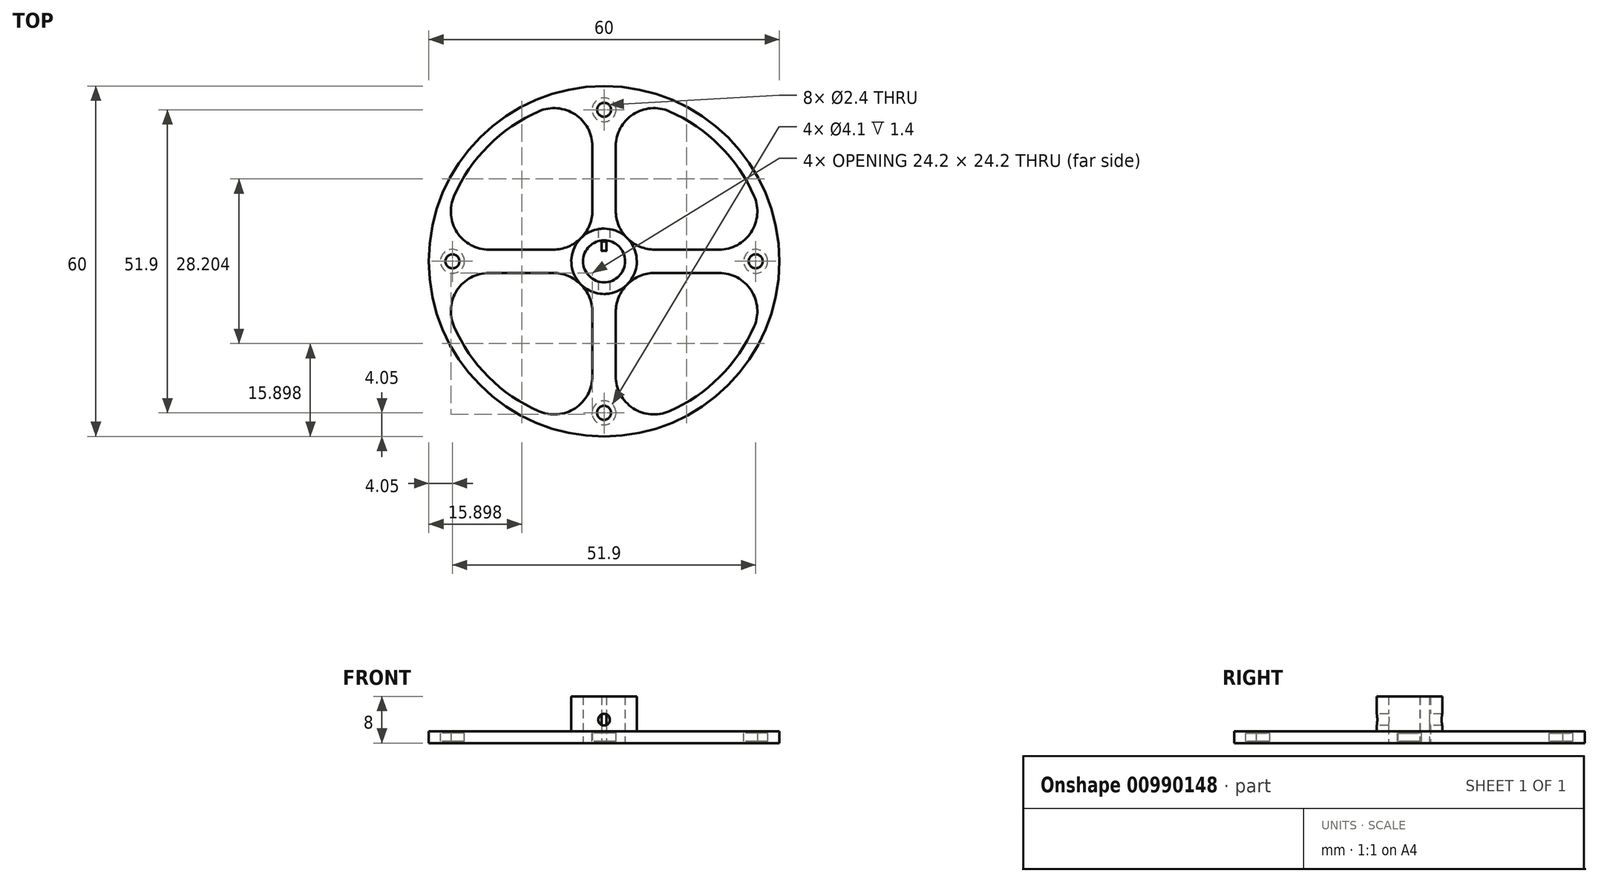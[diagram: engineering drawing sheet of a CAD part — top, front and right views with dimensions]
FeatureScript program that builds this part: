
annotation { "Feature Type Name" : "Feature", "Feature Type Description" : "" }
export const myFeature = defineFeature(function(context is Context, id is Id, definition is map)
    precondition{}
    {
        {
            assignVariable(context, id + "F0", {"name" : "Diameter", "anyValue" : 60 * mm});
        }
        {
            assignVariable(context, id + "F1", {"name" : "Buffer", "anyValue" : 2 * mm});
        }
        {
            assignVariable(context, id + "F2", {"name" : "BushingThickness", "anyValue" : 1.4 * mm});
        }
        {
            var Q0;
            Q0=qCreatedBy(makeId("Top.planeOp"),FACE);
            var sketch = newSketch(context, id + "F3", { "sketchPlane" : qUnion([Q0])});
            skCircle(sketch, "E0", {"center": v(0, 0) * mm, "radius": 30 * mm});
            skCircle(sketch, "E1", {"center": v(0, 0) * mm, "radius": 1.6 * mm});
            skCircle(sketch, "E2", {"center": v(0, 0) * mm, "radius": 3.6 * mm});
            skCircle(sketch, "E3", {"center": v(0, 0) * mm, "radius": 5.6 * mm});
            skCircle(sketch, "E4", {"center": v(-25.95, 0) * mm, "radius": 2.05 * mm});
            skCircle(sketch, "E5", {"center": v(-25.95, 0) * mm, "radius": 4.05 * mm});
            skLineSegment(sketch, "E6", {"start": v(-22.43, 2) * mm, "end": v(-5.23, 2) * mm});
            skLineSegment(sketch, "E7", {"start": v(-22.43, -2) * mm, "end": v(-5.23, -2) * mm});
            skCircle(sketch, "E8", {"center": v(0, 0) * mm, "radius": 28 * mm});
            skCircle(sketch, "E9", {"center": v(-19.69, 8.54) * mm, "radius": 6.54 * mm});
            skCircle(sketch, "E10", {"center": v(-8.7, 8.7) * mm, "radius": 6.7 * mm});
            skCircle(sketch, "E11", {"center": v(-19.69, -8.54) * mm, "radius": 6.54 * mm});
            skLineSegment(sketch, "E12", {"start": v(0, 0) * mm, "end": v(-21.21, 21.21) * mm});
            skCircle(sketch, "E13.1.0", {"center": v(-8.7, -8.7) * mm, "radius": 6.7 * mm});
            skCircle(sketch, "E13.1.1", {"center": v(-8.54, -19.69) * mm, "radius": 6.54 * mm});
            skLineSegment(sketch, "E13.1.2", {"start": v(0, 0) * mm, "end": v(-21.21, -21.21) * mm});
            skCircle(sketch, "E13.1.3", {"center": v(0, -25.95) * mm, "radius": 4.05 * mm});
            skCircle(sketch, "E13.1.4", {"center": v(0, -25.95) * mm, "radius": 2.05 * mm});
            skCircle(sketch, "E13.1.5", {"center": v(8.54, -19.69) * mm, "radius": 6.54 * mm});
            skLineSegment(sketch, "E13.1.6", {"start": v(2, -22.43) * mm, "end": v(2, -5.23) * mm});
            skLineSegment(sketch, "E13.1.7", {"start": v(-2, -22.43) * mm, "end": v(-2, -5.23) * mm});
            skCircle(sketch, "E13.2.0", {"center": v(8.7, -8.7) * mm, "radius": 6.7 * mm});
            skCircle(sketch, "E13.2.1", {"center": v(19.69, -8.54) * mm, "radius": 6.54 * mm});
            skLineSegment(sketch, "E13.2.2", {"start": v(0, 0) * mm, "end": v(21.21, -21.21) * mm});
            skCircle(sketch, "E13.2.3", {"center": v(25.95, 0) * mm, "radius": 4.05 * mm});
            skCircle(sketch, "E13.2.4", {"center": v(25.95, 0) * mm, "radius": 2.05 * mm});
            skCircle(sketch, "E13.2.5", {"center": v(19.69, 8.54) * mm, "radius": 6.54 * mm});
            skLineSegment(sketch, "E13.2.6", {"start": v(22.43, 2) * mm, "end": v(5.23, 2) * mm});
            skLineSegment(sketch, "E13.2.7", {"start": v(22.43, -2) * mm, "end": v(5.23, -2) * mm});
            skCircle(sketch, "E13.3.0", {"center": v(8.7, 8.7) * mm, "radius": 6.7 * mm});
            skCircle(sketch, "E13.3.1", {"center": v(8.54, 19.69) * mm, "radius": 6.54 * mm});
            skLineSegment(sketch, "E13.3.2", {"start": v(0, 0) * mm, "end": v(21.21, 21.21) * mm});
            skCircle(sketch, "E13.3.3", {"center": v(0, 25.95) * mm, "radius": 4.05 * mm});
            skCircle(sketch, "E13.3.4", {"center": v(0, 25.95) * mm, "radius": 2.05 * mm});
            skCircle(sketch, "E13.3.5", {"center": v(-8.54, 19.69) * mm, "radius": 6.54 * mm});
            skLineSegment(sketch, "E13.3.6", {"start": v(-2, 22.43) * mm, "end": v(-2, 5.23) * mm});
            skLineSegment(sketch, "E13.3.7", {"start": v(2, 22.43) * mm, "end": v(2, 5.23) * mm});
            skCircle(sketch, "E14", {"center": v(-25.95, 0) * mm, "radius": 1.2 * mm});
            skCircle(sketch, "E15.1.0", {"center": v(0, -25.95) * mm, "radius": 1.2 * mm});
            skCircle(sketch, "E15.2.0", {"center": v(25.95, 0) * mm, "radius": 1.2 * mm});
            skCircle(sketch, "E15.3.0", {"center": v(0, 25.95) * mm, "radius": 1.2 * mm});
            skSolve(sketch);
        }
        {
            var Q0;
            {var subQ4=sQuery(id+"F3.wireOp",EDGE,"E12");var subQ6=sQuery(id+"F3.wireOp",EDGE,"E0");var subQ8=makeQuery(id+"F3.imprint","INTERSECT",VERTEX,{"derivedFrom":[subQ6,subQ4]});Q0=makeQuery(id+"F3.imprint","IMPRINT",FACE,{"disambiguationData":[TD([[makeQuery(id+"F3.imprint","IMPRINT",EDGE,{"disambiguationData":[TD([[subQ8,-1.0]])],"derivedFrom":subQ6}),1.0]])]});}
            var Q1;
            {var subQ2=sQuery(id+"F3.wireOp",EDGE,"E13.1.2");var subQ6=sQuery(id+"F3.wireOp",EDGE,"E0");var subQ8=makeQuery(id+"F3.imprint","INTERSECT",VERTEX,{"derivedFrom":[subQ6,subQ2]});Q1=makeQuery(id+"F3.imprint","IMPRINT",FACE,{"disambiguationData":[TD([[makeQuery(id+"F3.imprint","IMPRINT",EDGE,{"disambiguationData":[TD([[subQ8,1.0]])],"derivedFrom":subQ6}),1.0]])]});}
            var Q2;
            {var subQ0=sQuery(id+"F3.wireOp",EDGE,"E8");var subQ1=sQuery(id+"F3.wireOp",EDGE,"E5");var subQ2=makeQuery(id+"F3.imprint","INTERSECT",VERTEX,{"disambiguationData":[OD(1.0)],"derivedFrom":[subQ1,subQ0]});Q2=makeQuery(id+"F3.imprint","IMPRINT",FACE,{"disambiguationData":[TD([[makeQuery(id+"F3.imprint","IMPRINT",EDGE,{"disambiguationData":[TD([[subQ2,-1.0]])],"derivedFrom":subQ1}),-1.0]])]});}
            var Q3;
            {var subQ0=sQuery(id+"F3.wireOp",EDGE,"E6");var subQ7=sQuery(id+"F3.wireOp",EDGE,"E3");var subQ8=makeQuery(id+"F3.imprint","INTERSECT",VERTEX,{"derivedFrom":[subQ7,subQ0]});Q3=makeQuery(id+"F3.imprint","IMPRINT",FACE,{"disambiguationData":[TD([[makeQuery(id+"F3.imprint","IMPRINT",EDGE,{"disambiguationData":[TD([[subQ8,-1.0]])],"derivedFrom":subQ7}),-1.0]])]});}
            var Q4;
            {var subQ0=sQuery(id+"F3.wireOp",EDGE,"E13.2.6");var subQ9=sQuery(id+"F3.wireOp",EDGE,"E3");var subQ10=makeQuery(id+"F3.imprint","INTERSECT",VERTEX,{"derivedFrom":[subQ9,subQ0]});Q4=makeQuery(id+"F3.imprint","IMPRINT",FACE,{"disambiguationData":[TD([[makeQuery(id+"F3.imprint","IMPRINT",EDGE,{"disambiguationData":[TD([[subQ10,1.0]])],"derivedFrom":subQ9}),-1.0]])]});}
            var Q5;
            {var subQ0=sQuery(id+"F3.wireOp",EDGE,"E13.1.6");var subQ3=sQuery(id+"F3.wireOp",EDGE,"E3");var subQ4=makeQuery(id+"F3.imprint","INTERSECT",VERTEX,{"derivedFrom":[subQ3,subQ0]});Q5=makeQuery(id+"F3.imprint","IMPRINT",FACE,{"disambiguationData":[TD([[makeQuery(id+"F3.imprint","IMPRINT",EDGE,{"disambiguationData":[TD([[subQ4,1.0]])],"derivedFrom":subQ3}),-1.0]])]});}
            var Q6;
            {var subQ0=sQuery(id+"F3.wireOp",EDGE,"E13.3.6");var subQ9=sQuery(id+"F3.wireOp",EDGE,"E3");var subQ10=makeQuery(id+"F3.imprint","INTERSECT",VERTEX,{"derivedFrom":[subQ9,subQ0]});Q6=makeQuery(id+"F3.imprint","IMPRINT",FACE,{"disambiguationData":[TD([[makeQuery(id+"F3.imprint","IMPRINT",EDGE,{"disambiguationData":[TD([[subQ10,1.0]])],"derivedFrom":subQ9}),-1.0]])]});}
            var Q7;
            {var subQ2=sQuery(id+"F3.wireOp",EDGE,"E12");var subQ4=sQuery(id+"F3.wireOp",EDGE,"E0");var subQ5=makeQuery(id+"F3.imprint","INTERSECT",VERTEX,{"derivedFrom":[subQ4,subQ2]});Q7=makeQuery(id+"F3.imprint","IMPRINT",FACE,{"disambiguationData":[TD([[makeQuery(id+"F3.imprint","IMPRINT",EDGE,{"disambiguationData":[TD([[subQ5,1.0]])],"derivedFrom":subQ4}),1.0]])]});}
            var Q8;
            {var subQ0=sQuery(id+"F3.wireOp",EDGE,"E13.3.2");var subQ1=sQuery(id+"F3.wireOp",EDGE,"E0");var subQ2=makeQuery(id+"F3.imprint","INTERSECT",VERTEX,{"derivedFrom":[subQ1,subQ0]});Q8=makeQuery(id+"F3.imprint","IMPRINT",FACE,{"disambiguationData":[TD([[makeQuery(id+"F3.imprint","IMPRINT",EDGE,{"disambiguationData":[TD([[subQ2,-1.0]])],"derivedFrom":subQ1}),1.0]])]});}
            var Q9;
            {var subQ0=sQuery(id+"F3.wireOp",EDGE,"E8");var subQ1=makeQuery(id+"F3.imprint","INTERSECT",VERTEX,{"derivedFrom":[subQ0,sQuery(id+"F3.wireOp",EDGE,"E13.3.4")]});Q9=makeQuery(id+"F3.imprint","IMPRINT",FACE,{"disambiguationData":[TD([[makeQuery(id+"F3.imprint","IMPRINT",EDGE,{"disambiguationData":[TD([[subQ1,1.0]])],"derivedFrom":subQ0}),-1.0]])]});}
            var Q10;
            {var subQ5=sQuery(id+"F3.wireOp",EDGE,"E13.3.4");Q10=makeQuery(id+"F3.imprint","IMPRINT",FACE,{"disambiguationData":[TD([[makeQuery(id+"F3.imprint","IMPRINT",EDGE,{"derivedFrom":subQ5}),-1.0]])]});}
            var Q11;
            {var subQ7=sQuery(id+"F3.wireOp",EDGE,"E4");Q11=makeQuery(id+"F3.imprint","IMPRINT",FACE,{"disambiguationData":[TD([[makeQuery(id+"F3.imprint","IMPRINT",EDGE,{"derivedFrom":subQ7}),-1.0]])]});}
            var Q12;
            {var subQ0=sQuery(id+"F3.wireOp",EDGE,"E5");var subQ1=makeQuery(id+"F3.imprint","INTERSECT",VERTEX,{"derivedFrom":[sQuery(id+"F3.wireOp",EDGE,"E0"),subQ0]});Q12=makeQuery(id+"F3.imprint","IMPRINT",FACE,{"disambiguationData":[TD([[makeQuery(id+"F3.imprint","IMPRINT",EDGE,{"disambiguationData":[TD([[subQ1,1.0]])],"derivedFrom":subQ0}),1.0]])]});}
            var Q13;
            Q13=makeQuery(id+"F3.imprint","IMPRINT",FACE,{"disambiguationData":[TD([[makeQuery(id+"F3.imprint","IMPRINT",EDGE,{"derivedFrom":sQuery(id+"F3.wireOp",EDGE,"E4")}),1.0]])]});
            var Q14;
            {var subQ1=sQuery(id+"F3.wireOp",EDGE,"E0");var subQ6=sQuery(id+"F3.wireOp",EDGE,"E13.2.2");var subQ8=makeQuery(id+"F3.imprint","INTERSECT",VERTEX,{"derivedFrom":[subQ1,subQ6]});Q14=makeQuery(id+"F3.imprint","IMPRINT",FACE,{"disambiguationData":[TD([[makeQuery(id+"F3.imprint","IMPRINT",EDGE,{"disambiguationData":[TD([[subQ8,1.0]])],"derivedFrom":subQ1}),1.0]])]});}
            var Q15;
            {var subQ0=sQuery(id+"F3.wireOp",EDGE,"E13.1.2");var subQ1=sQuery(id+"F3.wireOp",EDGE,"E0");var subQ2=makeQuery(id+"F3.imprint","INTERSECT",VERTEX,{"derivedFrom":[subQ1,subQ0]});Q15=makeQuery(id+"F3.imprint","IMPRINT",FACE,{"disambiguationData":[TD([[makeQuery(id+"F3.imprint","IMPRINT",EDGE,{"disambiguationData":[TD([[subQ2,-1.0]])],"derivedFrom":subQ1}),1.0]])]});}
            var Q16;
            {var subQ4=sQuery(id+"F3.wireOp",EDGE,"E13.1.4");Q16=makeQuery(id+"F3.imprint","IMPRINT",FACE,{"disambiguationData":[TD([[makeQuery(id+"F3.imprint","IMPRINT",EDGE,{"derivedFrom":subQ4}),-1.0]])]});}
            var Q17;
            {var subQ0=sQuery(id+"F3.wireOp",EDGE,"E8");var subQ1=makeQuery(id+"F3.imprint","INTERSECT",VERTEX,{"derivedFrom":[subQ0,sQuery(id+"F3.wireOp",EDGE,"E13.1.4")]});Q17=makeQuery(id+"F3.imprint","IMPRINT",FACE,{"disambiguationData":[TD([[makeQuery(id+"F3.imprint","IMPRINT",EDGE,{"disambiguationData":[TD([[subQ1,1.0]])],"derivedFrom":subQ0}),-1.0]])]});}
            var Q18;
            {var subQ4=sQuery(id+"F3.wireOp",EDGE,"E13.2.4");Q18=makeQuery(id+"F3.imprint","IMPRINT",FACE,{"disambiguationData":[TD([[makeQuery(id+"F3.imprint","IMPRINT",EDGE,{"derivedFrom":subQ4}),-1.0]])]});}
            var Q19;
            {var subQ0=sQuery(id+"F3.wireOp",EDGE,"E8");var subQ1=makeQuery(id+"F3.imprint","INTERSECT",VERTEX,{"derivedFrom":[subQ0,sQuery(id+"F3.wireOp",EDGE,"E13.2.4")]});Q19=makeQuery(id+"F3.imprint","IMPRINT",FACE,{"disambiguationData":[TD([[makeQuery(id+"F3.imprint","IMPRINT",EDGE,{"disambiguationData":[TD([[subQ1,-1.0]])],"derivedFrom":subQ0}),-1.0]])]});}
            var Q20;
            Q20=makeQuery(id+"F3.imprint","IMPRINT",FACE,{"disambiguationData":[TD([[makeQuery(id+"F3.imprint","IMPRINT",EDGE,{"derivedFrom":sQuery(id+"F3.wireOp",EDGE,"E13.3.4")}),1.0]])]});
            var Q21;
            Q21=makeQuery(id+"F3.imprint","IMPRINT",FACE,{"disambiguationData":[TD([[makeQuery(id+"F3.imprint","IMPRINT",EDGE,{"derivedFrom":sQuery(id+"F3.wireOp",EDGE,"E13.1.4")}),1.0]])]});
            var Q22;
            Q22=makeQuery(id+"F3.imprint","IMPRINT",FACE,{"disambiguationData":[TD([[makeQuery(id+"F3.imprint","IMPRINT",EDGE,{"derivedFrom":sQuery(id+"F3.wireOp",EDGE,"E13.2.4")}),1.0]])]});
            var Q23;
            {var subQ0=sQuery(id+"F3.wireOp",EDGE,"E13.2.2");var subQ1=sQuery(id+"F3.wireOp",EDGE,"E0");var subQ2=makeQuery(id+"F3.imprint","INTERSECT",VERTEX,{"derivedFrom":[subQ1,subQ0]});Q23=makeQuery(id+"F3.imprint","IMPRINT",FACE,{"disambiguationData":[TD([[makeQuery(id+"F3.imprint","IMPRINT",EDGE,{"disambiguationData":[TD([[subQ2,-1.0]])],"derivedFrom":subQ1}),1.0]])]});}
            var Q24;
            {var subQ2=sQuery(id+"F3.wireOp",EDGE,"E13.3.2");var subQ4=sQuery(id+"F3.wireOp",EDGE,"E0");var subQ5=makeQuery(id+"F3.imprint","INTERSECT",VERTEX,{"derivedFrom":[subQ4,subQ2]});Q24=makeQuery(id+"F3.imprint","IMPRINT",FACE,{"disambiguationData":[TD([[makeQuery(id+"F3.imprint","IMPRINT",EDGE,{"disambiguationData":[TD([[subQ5,1.0]])],"derivedFrom":subQ4}),1.0]])]});}
            var Q25;
            {var subQ3=sQuery(id+"F3.wireOp",EDGE,"E13.3.2");var subQ5=sQuery(id+"F3.wireOp",EDGE,"E2");var subQ6=makeQuery(id+"F3.imprint","INTERSECT",VERTEX,{"derivedFrom":[subQ5,subQ3]});Q25=makeQuery(id+"F3.imprint","IMPRINT",FACE,{"disambiguationData":[TD([[makeQuery(id+"F3.imprint","IMPRINT",EDGE,{"disambiguationData":[TD([[subQ6,1.0]])],"derivedFrom":subQ5}),-1.0]])]});}
            var Q26;
            {var subQ2=sQuery(id+"F3.wireOp",EDGE,"E12");var subQ7=sQuery(id+"F3.wireOp",EDGE,"E2");var subQ8=makeQuery(id+"F3.imprint","INTERSECT",VERTEX,{"derivedFrom":[subQ7,subQ2]});Q26=makeQuery(id+"F3.imprint","IMPRINT",FACE,{"disambiguationData":[TD([[makeQuery(id+"F3.imprint","IMPRINT",EDGE,{"disambiguationData":[TD([[subQ8,1.0]])],"derivedFrom":subQ7}),-1.0]])]});}
            var Q27;
            {var subQ5=sQuery(id+"F3.wireOp",EDGE,"E12");var subQ7=sQuery(id+"F3.wireOp",EDGE,"E2");var subQ8=makeQuery(id+"F3.imprint","INTERSECT",VERTEX,{"derivedFrom":[subQ7,subQ5]});Q27=makeQuery(id+"F3.imprint","IMPRINT",FACE,{"disambiguationData":[TD([[makeQuery(id+"F3.imprint","IMPRINT",EDGE,{"disambiguationData":[TD([[subQ8,-1.0]])],"derivedFrom":subQ7}),-1.0]])]});}
            var Q28;
            {var subQ4=sQuery(id+"F3.wireOp",EDGE,"E13.1.2");var subQ5=sQuery(id+"F3.wireOp",EDGE,"E2");var subQ6=makeQuery(id+"F3.imprint","INTERSECT",VERTEX,{"derivedFrom":[subQ5,subQ4]});Q28=makeQuery(id+"F3.imprint","IMPRINT",FACE,{"disambiguationData":[TD([[makeQuery(id+"F3.imprint","IMPRINT",EDGE,{"disambiguationData":[TD([[subQ6,-1.0]])],"derivedFrom":subQ5}),-1.0]])]});}
            var Q29;
            {var subQ0=sQuery(id+"F3.wireOp",EDGE,"E13.1.2");var subQ1=sQuery(id+"F3.wireOp",EDGE,"E1");var subQ2=makeQuery(id+"F3.imprint","INTERSECT",VERTEX,{"derivedFrom":[subQ1,subQ0]});Q29=makeQuery(id+"F3.imprint","IMPRINT",FACE,{"disambiguationData":[TD([[makeQuery(id+"F3.imprint","IMPRINT",EDGE,{"disambiguationData":[TD([[subQ2,-1.0]])],"derivedFrom":subQ1}),-1.0]])]});}
            var Q30;
            {var subQ0=sQuery(id+"F3.wireOp",EDGE,"E13.3.2");var subQ1=sQuery(id+"F3.wireOp",EDGE,"E1");var subQ2=makeQuery(id+"F3.imprint","INTERSECT",VERTEX,{"derivedFrom":[subQ1,subQ0]});Q30=makeQuery(id+"F3.imprint","IMPRINT",FACE,{"disambiguationData":[TD([[makeQuery(id+"F3.imprint","IMPRINT",EDGE,{"disambiguationData":[TD([[subQ2,1.0]])],"derivedFrom":subQ1}),-1.0]])]});}
            var Q31;
            {var subQ0=sQuery(id+"F3.wireOp",EDGE,"E12");var subQ1=sQuery(id+"F3.wireOp",EDGE,"E1");var subQ2=makeQuery(id+"F3.imprint","INTERSECT",VERTEX,{"derivedFrom":[subQ1,subQ0]});Q31=makeQuery(id+"F3.imprint","IMPRINT",FACE,{"disambiguationData":[TD([[makeQuery(id+"F3.imprint","IMPRINT",EDGE,{"disambiguationData":[TD([[subQ2,1.0]])],"derivedFrom":subQ1}),-1.0]])]});}
            var Q32;
            {var subQ0=sQuery(id+"F3.wireOp",EDGE,"E12");var subQ1=sQuery(id+"F3.wireOp",EDGE,"E1");var subQ2=makeQuery(id+"F3.imprint","INTERSECT",VERTEX,{"derivedFrom":[subQ1,subQ0]});Q32=makeQuery(id+"F3.imprint","IMPRINT",FACE,{"disambiguationData":[TD([[makeQuery(id+"F3.imprint","IMPRINT",EDGE,{"disambiguationData":[TD([[subQ2,-1.0]])],"derivedFrom":subQ1}),-1.0]])]});}
            var Q33;
            {var subQ0=sQuery(id+"F3.wireOp",EDGE,"E12");var subQ1=sQuery(id+"F3.wireOp",EDGE,"E1");var subQ2=makeQuery(id+"F3.imprint","INTERSECT",VERTEX,{"derivedFrom":[subQ1,subQ0]});Q33=makeQuery(id+"F3.imprint","IMPRINT",FACE,{"disambiguationData":[TD([[makeQuery(id+"F3.imprint","IMPRINT",EDGE,{"disambiguationData":[TD([[subQ2,-1.0]])],"derivedFrom":subQ1}),1.0]])]});}
            var Q34;
            {var subQ0=sQuery(id+"F3.wireOp",EDGE,"E12");var subQ1=sQuery(id+"F3.wireOp",EDGE,"E1");var subQ2=makeQuery(id+"F3.imprint","INTERSECT",VERTEX,{"derivedFrom":[subQ1,subQ0]});Q34=makeQuery(id+"F3.imprint","IMPRINT",FACE,{"disambiguationData":[TD([[makeQuery(id+"F3.imprint","IMPRINT",EDGE,{"disambiguationData":[TD([[subQ2,1.0]])],"derivedFrom":subQ1}),1.0]])]});}
            var Q35;
            {var subQ0=sQuery(id+"F3.wireOp",EDGE,"E13.3.2");var subQ1=sQuery(id+"F3.wireOp",EDGE,"E1");var subQ2=makeQuery(id+"F3.imprint","INTERSECT",VERTEX,{"derivedFrom":[subQ1,subQ0]});Q35=makeQuery(id+"F3.imprint","IMPRINT",FACE,{"disambiguationData":[TD([[makeQuery(id+"F3.imprint","IMPRINT",EDGE,{"disambiguationData":[TD([[subQ2,1.0]])],"derivedFrom":subQ1}),1.0]])]});}
            var Q36;
            {var subQ0=sQuery(id+"F3.wireOp",EDGE,"E13.1.2");var subQ1=sQuery(id+"F3.wireOp",EDGE,"E1");var subQ2=makeQuery(id+"F3.imprint","INTERSECT",VERTEX,{"derivedFrom":[subQ1,subQ0]});Q36=makeQuery(id+"F3.imprint","IMPRINT",FACE,{"disambiguationData":[TD([[makeQuery(id+"F3.imprint","IMPRINT",EDGE,{"disambiguationData":[TD([[subQ2,-1.0]])],"derivedFrom":subQ1}),1.0]])]});}
            var Q37;
            {var subQ0=sQuery(id+"F3.wireOp",EDGE,"E6");var subQ1=sQuery(id+"F3.wireOp",EDGE,"E3");var subQ2=makeQuery(id+"F3.imprint","INTERSECT",VERTEX,{"derivedFrom":[subQ1,subQ0]});Q37=makeQuery(id+"F3.imprint","IMPRINT",FACE,{"disambiguationData":[TD([[makeQuery(id+"F3.imprint","IMPRINT",EDGE,{"disambiguationData":[TD([[subQ2,1.0]])],"derivedFrom":subQ0}),1.0]])]});}
            var Q38;
            {var subQ0=sQuery(id+"F3.wireOp",EDGE,"E13.3.6");var subQ1=sQuery(id+"F3.wireOp",EDGE,"E3");var subQ2=makeQuery(id+"F3.imprint","INTERSECT",VERTEX,{"derivedFrom":[subQ1,subQ0]});Q38=makeQuery(id+"F3.imprint","IMPRINT",FACE,{"disambiguationData":[TD([[makeQuery(id+"F3.imprint","IMPRINT",EDGE,{"disambiguationData":[TD([[subQ2,1.0]])],"derivedFrom":subQ0}),-1.0]])]});}
            var Q39;
            {var subQ0=sQuery(id+"F3.wireOp",EDGE,"E9");var subQ1=sQuery(id+"F3.wireOp",EDGE,"E5");var subQ2=makeQuery(id+"F3.imprint","INTERSECT",VERTEX,{"derivedFrom":[subQ1,subQ0]});Q39=makeQuery(id+"F3.imprint","IMPRINT",FACE,{"disambiguationData":[TD([[makeQuery(id+"F3.imprint","IMPRINT",EDGE,{"disambiguationData":[TD([[subQ2,-1.0]])],"derivedFrom":subQ1}),-1.0]])]});}
            var Q40;
            {var subQ0=sQuery(id+"F3.wireOp",EDGE,"E6");var subQ1=sQuery(id+"F3.wireOp",EDGE,"E5");var subQ2=makeQuery(id+"F3.imprint","INTERSECT",VERTEX,{"derivedFrom":[subQ1,subQ0]});Q40=makeQuery(id+"F3.imprint","IMPRINT",FACE,{"disambiguationData":[TD([[makeQuery(id+"F3.imprint","IMPRINT",EDGE,{"disambiguationData":[TD([[subQ2,-1.0]])],"derivedFrom":subQ1}),-1.0]])]});}
            var Q41;
            {var subQ0=sQuery(id+"F3.wireOp",EDGE,"E13.3.3");var subQ1=sQuery(id+"F3.wireOp",EDGE,"E8");var subQ2=makeQuery(id+"F3.imprint","INTERSECT",VERTEX,{"disambiguationData":[OD(1.0)],"derivedFrom":[subQ1,subQ0]});Q41=makeQuery(id+"F3.imprint","IMPRINT",FACE,{"disambiguationData":[TD([[makeQuery(id+"F3.imprint","IMPRINT",EDGE,{"disambiguationData":[TD([[subQ2,-1.0]])],"derivedFrom":subQ1}),1.0]])]});}
            var Q42;
            {var subQ0=sQuery(id+"F3.wireOp",EDGE,"E13.3.6");var subQ1=sQuery(id+"F3.wireOp",EDGE,"E13.3.3");var subQ2=makeQuery(id+"F3.imprint","INTERSECT",VERTEX,{"derivedFrom":[subQ1,subQ0]});Q42=makeQuery(id+"F3.imprint","IMPRINT",FACE,{"disambiguationData":[TD([[makeQuery(id+"F3.imprint","IMPRINT",EDGE,{"disambiguationData":[TD([[subQ2,1.0]])],"derivedFrom":subQ1}),-1.0]])]});}
            var Q43;
            {var subQ0=sQuery(id+"F3.wireOp",EDGE,"E13.3.1");var subQ1=sQuery(id+"F3.wireOp",EDGE,"E8");var subQ2=makeQuery(id+"F3.imprint","INTERSECT",VERTEX,{"derivedFrom":[subQ1,subQ0]});Q43=makeQuery(id+"F3.imprint","IMPRINT",FACE,{"disambiguationData":[TD([[makeQuery(id+"F3.imprint","IMPRINT",EDGE,{"disambiguationData":[TD([[subQ2,-1.0]])],"derivedFrom":subQ1}),1.0]])]});}
            var Q44;
            {var subQ0=sQuery(id+"F3.wireOp",EDGE,"E13.3.3");var subQ1=sQuery(id+"F3.wireOp",EDGE,"E13.3.1");var subQ2=makeQuery(id+"F3.imprint","INTERSECT",VERTEX,{"derivedFrom":[subQ1,subQ0]});Q44=makeQuery(id+"F3.imprint","IMPRINT",FACE,{"disambiguationData":[TD([[makeQuery(id+"F3.imprint","IMPRINT",EDGE,{"disambiguationData":[TD([[subQ2,-1.0]])],"derivedFrom":subQ1}),-1.0]])]});}
            var Q45;
            {var subQ0=sQuery(id+"F3.wireOp",EDGE,"E13.2.3");var subQ1=sQuery(id+"F3.wireOp",EDGE,"E8");var subQ2=makeQuery(id+"F3.imprint","INTERSECT",VERTEX,{"disambiguationData":[OD(0.0)],"derivedFrom":[subQ1,subQ0]});Q45=makeQuery(id+"F3.imprint","IMPRINT",FACE,{"disambiguationData":[TD([[makeQuery(id+"F3.imprint","IMPRINT",EDGE,{"disambiguationData":[TD([[subQ2,-1.0]])],"derivedFrom":subQ1}),1.0]])]});}
            var Q46;
            {var subQ0=sQuery(id+"F3.wireOp",EDGE,"E13.2.6");var subQ1=sQuery(id+"F3.wireOp",EDGE,"E13.2.3");var subQ2=makeQuery(id+"F3.imprint","INTERSECT",VERTEX,{"derivedFrom":[subQ1,subQ0]});Q46=makeQuery(id+"F3.imprint","IMPRINT",FACE,{"disambiguationData":[TD([[makeQuery(id+"F3.imprint","IMPRINT",EDGE,{"disambiguationData":[TD([[subQ2,1.0]])],"derivedFrom":subQ1}),-1.0]])]});}
            var Q47;
            {var subQ0=sQuery(id+"F3.wireOp",EDGE,"E13.2.6");var subQ1=sQuery(id+"F3.wireOp",EDGE,"E3");var subQ2=makeQuery(id+"F3.imprint","INTERSECT",VERTEX,{"derivedFrom":[subQ1,subQ0]});Q47=makeQuery(id+"F3.imprint","IMPRINT",FACE,{"disambiguationData":[TD([[makeQuery(id+"F3.imprint","IMPRINT",EDGE,{"disambiguationData":[TD([[subQ2,1.0]])],"derivedFrom":subQ0}),-1.0]])]});}
            var Q48;
            {var subQ0=sQuery(id+"F3.wireOp",EDGE,"E13.3.7");var subQ1=sQuery(id+"F3.wireOp",EDGE,"E3");var subQ2=makeQuery(id+"F3.imprint","INTERSECT",VERTEX,{"derivedFrom":[subQ1,subQ0]});Q48=makeQuery(id+"F3.imprint","IMPRINT",FACE,{"disambiguationData":[TD([[makeQuery(id+"F3.imprint","IMPRINT",EDGE,{"disambiguationData":[TD([[subQ2,1.0]])],"derivedFrom":subQ0}),1.0]])]});}
            var Q49;
            {var subQ0=sQuery(id+"F3.wireOp",EDGE,"E7");var subQ1=sQuery(id+"F3.wireOp",EDGE,"E5");var subQ2=makeQuery(id+"F3.imprint","INTERSECT",VERTEX,{"derivedFrom":[subQ1,subQ0]});Q49=makeQuery(id+"F3.imprint","IMPRINT",FACE,{"disambiguationData":[TD([[makeQuery(id+"F3.imprint","IMPRINT",EDGE,{"disambiguationData":[TD([[subQ2,1.0]])],"derivedFrom":subQ1}),-1.0]])]});}
            var Q50;
            {var subQ0=sQuery(id+"F3.wireOp",EDGE,"E7");var subQ1=sQuery(id+"F3.wireOp",EDGE,"E3");var subQ2=makeQuery(id+"F3.imprint","INTERSECT",VERTEX,{"derivedFrom":[subQ1,subQ0]});Q50=makeQuery(id+"F3.imprint","IMPRINT",FACE,{"disambiguationData":[TD([[makeQuery(id+"F3.imprint","IMPRINT",EDGE,{"disambiguationData":[TD([[subQ2,1.0]])],"derivedFrom":subQ0}),-1.0]])]});}
            var Q51;
            {var subQ0=sQuery(id+"F3.wireOp",EDGE,"E13.1.7");var subQ1=sQuery(id+"F3.wireOp",EDGE,"E3");var subQ2=makeQuery(id+"F3.imprint","INTERSECT",VERTEX,{"derivedFrom":[subQ1,subQ0]});Q51=makeQuery(id+"F3.imprint","IMPRINT",FACE,{"disambiguationData":[TD([[makeQuery(id+"F3.imprint","IMPRINT",EDGE,{"disambiguationData":[TD([[subQ2,1.0]])],"derivedFrom":subQ0}),1.0]])]});}
            var Q52;
            {var subQ0=sQuery(id+"F3.wireOp",EDGE,"E13.1.1");var subQ1=sQuery(id+"F3.wireOp",EDGE,"E8");var subQ2=makeQuery(id+"F3.imprint","INTERSECT",VERTEX,{"derivedFrom":[subQ1,subQ0]});Q52=makeQuery(id+"F3.imprint","IMPRINT",FACE,{"disambiguationData":[TD([[makeQuery(id+"F3.imprint","IMPRINT",EDGE,{"disambiguationData":[TD([[subQ2,-1.0]])],"derivedFrom":subQ1}),1.0]])]});}
            var Q53;
            {var subQ0=sQuery(id+"F3.wireOp",EDGE,"E13.1.3");var subQ1=sQuery(id+"F3.wireOp",EDGE,"E13.1.1");var subQ2=makeQuery(id+"F3.imprint","INTERSECT",VERTEX,{"derivedFrom":[subQ1,subQ0]});Q53=makeQuery(id+"F3.imprint","IMPRINT",FACE,{"disambiguationData":[TD([[makeQuery(id+"F3.imprint","IMPRINT",EDGE,{"disambiguationData":[TD([[subQ2,-1.0]])],"derivedFrom":subQ1}),-1.0]])]});}
            var Q54;
            {var subQ0=sQuery(id+"F3.wireOp",EDGE,"E13.1.3");var subQ1=sQuery(id+"F3.wireOp",EDGE,"E8");var subQ2=makeQuery(id+"F3.imprint","INTERSECT",VERTEX,{"disambiguationData":[OD(1.0)],"derivedFrom":[subQ1,subQ0]});Q54=makeQuery(id+"F3.imprint","IMPRINT",FACE,{"disambiguationData":[TD([[makeQuery(id+"F3.imprint","IMPRINT",EDGE,{"disambiguationData":[TD([[subQ2,-1.0]])],"derivedFrom":subQ1}),1.0]])]});}
            var Q55;
            {var subQ0=sQuery(id+"F3.wireOp",EDGE,"E13.1.6");var subQ1=sQuery(id+"F3.wireOp",EDGE,"E13.1.3");var subQ2=makeQuery(id+"F3.imprint","INTERSECT",VERTEX,{"derivedFrom":[subQ1,subQ0]});Q55=makeQuery(id+"F3.imprint","IMPRINT",FACE,{"disambiguationData":[TD([[makeQuery(id+"F3.imprint","IMPRINT",EDGE,{"disambiguationData":[TD([[subQ2,1.0]])],"derivedFrom":subQ1}),-1.0]])]});}
            var Q56;
            {var subQ0=sQuery(id+"F3.wireOp",EDGE,"E13.2.3");var subQ1=sQuery(id+"F3.wireOp",EDGE,"E13.2.1");var subQ2=makeQuery(id+"F3.imprint","INTERSECT",VERTEX,{"derivedFrom":[subQ1,subQ0]});Q56=makeQuery(id+"F3.imprint","IMPRINT",FACE,{"disambiguationData":[TD([[makeQuery(id+"F3.imprint","IMPRINT",EDGE,{"disambiguationData":[TD([[subQ2,-1.0]])],"derivedFrom":subQ1}),-1.0]])]});}
            var Q57;
            {var subQ0=sQuery(id+"F3.wireOp",EDGE,"E13.2.1");var subQ1=sQuery(id+"F3.wireOp",EDGE,"E8");var subQ2=makeQuery(id+"F3.imprint","INTERSECT",VERTEX,{"derivedFrom":[subQ1,subQ0]});Q57=makeQuery(id+"F3.imprint","IMPRINT",FACE,{"disambiguationData":[TD([[makeQuery(id+"F3.imprint","IMPRINT",EDGE,{"disambiguationData":[TD([[subQ2,-1.0]])],"derivedFrom":subQ1}),1.0]])]});}
            var Q58;
            {var subQ0=sQuery(id+"F3.wireOp",EDGE,"E13.2.7");var subQ1=sQuery(id+"F3.wireOp",EDGE,"E3");var subQ2=makeQuery(id+"F3.imprint","INTERSECT",VERTEX,{"derivedFrom":[subQ1,subQ0]});Q58=makeQuery(id+"F3.imprint","IMPRINT",FACE,{"disambiguationData":[TD([[makeQuery(id+"F3.imprint","IMPRINT",EDGE,{"disambiguationData":[TD([[subQ2,1.0]])],"derivedFrom":subQ0}),1.0]])]});}
            var Q59;
            {var subQ0=sQuery(id+"F3.wireOp",EDGE,"E13.1.6");var subQ1=sQuery(id+"F3.wireOp",EDGE,"E3");var subQ2=makeQuery(id+"F3.imprint","INTERSECT",VERTEX,{"derivedFrom":[subQ1,subQ0]});Q59=makeQuery(id+"F3.imprint","IMPRINT",FACE,{"disambiguationData":[TD([[makeQuery(id+"F3.imprint","IMPRINT",EDGE,{"disambiguationData":[TD([[subQ2,1.0]])],"derivedFrom":subQ0}),-1.0]])]});}
            extrude(context, id + "F4", {"entities" : qUnion([Q0, Q1, Q2, Q3, Q4, Q5, Q6, Q7, Q8, Q9, Q10, Q11, Q12, Q13, Q14, Q15, Q16, Q17, Q18, Q19, Q20, Q21, Q22, Q23, Q24, Q25, Q26, Q27, Q28, Q29, Q30, Q31, Q32, Q33, Q34, Q35, Q36, Q37, Q38, Q39, Q40, Q41, Q42, Q43, Q44, Q45, Q46, Q47, Q48, Q49, Q50, Q51, Q52, Q53, Q54, Q55, Q56, Q57, Q58, Q59]), "depth" : getVariable(context, 'Buffer') / 2, "offsetDistance" : 25 * mm, "hasSecondDirection" : true, "secondDirectionOppositeDirection" : true, "secondDirectionDepth" : getVariable(context, 'Buffer') / 2});
        }
        {
            var Q0;
            {var subQ0=sQuery(id+"F3.wireOp",EDGE,"E12");var subQ1=sQuery(id+"F3.wireOp",EDGE,"E1");var subQ2=makeQuery(id+"F3.imprint","INTERSECT",VERTEX,{"derivedFrom":[subQ1,subQ0]});Q0=makeQuery(id+"F3.imprint","IMPRINT",FACE,{"disambiguationData":[TD([[makeQuery(id+"F3.imprint","IMPRINT",EDGE,{"disambiguationData":[TD([[subQ2,1.0]])],"derivedFrom":subQ1}),1.0]])]});}
            var Q1;
            {var subQ0=sQuery(id+"F3.wireOp",EDGE,"E13.3.2");var subQ1=sQuery(id+"F3.wireOp",EDGE,"E1");var subQ2=makeQuery(id+"F3.imprint","INTERSECT",VERTEX,{"derivedFrom":[subQ1,subQ0]});Q1=makeQuery(id+"F3.imprint","IMPRINT",FACE,{"disambiguationData":[TD([[makeQuery(id+"F3.imprint","IMPRINT",EDGE,{"disambiguationData":[TD([[subQ2,1.0]])],"derivedFrom":subQ1}),1.0]])]});}
            var Q2;
            {var subQ0=sQuery(id+"F3.wireOp",EDGE,"E13.1.2");var subQ1=sQuery(id+"F3.wireOp",EDGE,"E1");var subQ2=makeQuery(id+"F3.imprint","INTERSECT",VERTEX,{"derivedFrom":[subQ1,subQ0]});Q2=makeQuery(id+"F3.imprint","IMPRINT",FACE,{"disambiguationData":[TD([[makeQuery(id+"F3.imprint","IMPRINT",EDGE,{"disambiguationData":[TD([[subQ2,-1.0]])],"derivedFrom":subQ1}),1.0]])]});}
            var Q3;
            {var subQ0=sQuery(id+"F3.wireOp",EDGE,"E12");var subQ1=sQuery(id+"F3.wireOp",EDGE,"E1");var subQ2=makeQuery(id+"F3.imprint","INTERSECT",VERTEX,{"derivedFrom":[subQ1,subQ0]});Q3=makeQuery(id+"F3.imprint","IMPRINT",FACE,{"disambiguationData":[TD([[makeQuery(id+"F3.imprint","IMPRINT",EDGE,{"disambiguationData":[TD([[subQ2,-1.0]])],"derivedFrom":subQ1}),1.0]])]});}
            var Q4;
            {var subQ0=sQuery(id+"F3.wireOp",EDGE,"E12");var subQ1=sQuery(id+"F3.wireOp",EDGE,"E1");var subQ2=makeQuery(id+"F3.imprint","INTERSECT",VERTEX,{"derivedFrom":[subQ1,subQ0]});Q4=makeQuery(id+"F3.imprint","IMPRINT",FACE,{"disambiguationData":[TD([[makeQuery(id+"F3.imprint","IMPRINT",EDGE,{"disambiguationData":[TD([[subQ2,-1.0]])],"derivedFrom":subQ1}),-1.0]])]});}
            var Q5;
            {var subQ0=sQuery(id+"F3.wireOp",EDGE,"E12");var subQ1=sQuery(id+"F3.wireOp",EDGE,"E1");var subQ2=makeQuery(id+"F3.imprint","INTERSECT",VERTEX,{"derivedFrom":[subQ1,subQ0]});Q5=makeQuery(id+"F3.imprint","IMPRINT",FACE,{"disambiguationData":[TD([[makeQuery(id+"F3.imprint","IMPRINT",EDGE,{"disambiguationData":[TD([[subQ2,1.0]])],"derivedFrom":subQ1}),-1.0]])]});}
            var Q6;
            {var subQ0=sQuery(id+"F3.wireOp",EDGE,"E13.3.2");var subQ1=sQuery(id+"F3.wireOp",EDGE,"E1");var subQ2=makeQuery(id+"F3.imprint","INTERSECT",VERTEX,{"derivedFrom":[subQ1,subQ0]});Q6=makeQuery(id+"F3.imprint","IMPRINT",FACE,{"disambiguationData":[TD([[makeQuery(id+"F3.imprint","IMPRINT",EDGE,{"disambiguationData":[TD([[subQ2,1.0]])],"derivedFrom":subQ1}),-1.0]])]});}
            var Q7;
            {var subQ0=sQuery(id+"F3.wireOp",EDGE,"E13.1.2");var subQ1=sQuery(id+"F3.wireOp",EDGE,"E1");var subQ2=makeQuery(id+"F3.imprint","INTERSECT",VERTEX,{"derivedFrom":[subQ1,subQ0]});Q7=makeQuery(id+"F3.imprint","IMPRINT",FACE,{"disambiguationData":[TD([[makeQuery(id+"F3.imprint","IMPRINT",EDGE,{"disambiguationData":[TD([[subQ2,-1.0]])],"derivedFrom":subQ1}),-1.0]])]});}
            extrude(context, id + "F5", {"entities" : qUnion([Q0, Q1, Q2, Q3, Q4, Q5, Q6, Q7]), "operationType" : NewBodyOperationType.REMOVE, "depth" : getVariable(context, 'Buffer') / 2, "offsetDistance" : 25 * mm, "hasSecondDirection" : true, "secondDirectionOppositeDirection" : true, "secondDirectionDepth" : getVariable(context, 'Buffer') / 2});
        }
        {
            var Q0;
            {var subQ2=sQuery(id+"F3.wireOp",EDGE,"E12");var subQ7=sQuery(id+"F3.wireOp",EDGE,"E2");var subQ8=makeQuery(id+"F3.imprint","INTERSECT",VERTEX,{"derivedFrom":[subQ7,subQ2]});Q0=makeQuery(id+"F3.imprint","IMPRINT",FACE,{"disambiguationData":[TD([[makeQuery(id+"F3.imprint","IMPRINT",EDGE,{"disambiguationData":[TD([[subQ8,1.0]])],"derivedFrom":subQ7}),-1.0]])]});}
            var Q1;
            {var subQ5=sQuery(id+"F3.wireOp",EDGE,"E12");var subQ7=sQuery(id+"F3.wireOp",EDGE,"E2");var subQ8=makeQuery(id+"F3.imprint","INTERSECT",VERTEX,{"derivedFrom":[subQ7,subQ5]});Q1=makeQuery(id+"F3.imprint","IMPRINT",FACE,{"disambiguationData":[TD([[makeQuery(id+"F3.imprint","IMPRINT",EDGE,{"disambiguationData":[TD([[subQ8,-1.0]])],"derivedFrom":subQ7}),-1.0]])]});}
            var Q2;
            {var subQ4=sQuery(id+"F3.wireOp",EDGE,"E13.1.2");var subQ5=sQuery(id+"F3.wireOp",EDGE,"E2");var subQ6=makeQuery(id+"F3.imprint","INTERSECT",VERTEX,{"derivedFrom":[subQ5,subQ4]});Q2=makeQuery(id+"F3.imprint","IMPRINT",FACE,{"disambiguationData":[TD([[makeQuery(id+"F3.imprint","IMPRINT",EDGE,{"disambiguationData":[TD([[subQ6,-1.0]])],"derivedFrom":subQ5}),-1.0]])]});}
            var Q3;
            {var subQ3=sQuery(id+"F3.wireOp",EDGE,"E13.3.2");var subQ5=sQuery(id+"F3.wireOp",EDGE,"E2");var subQ6=makeQuery(id+"F3.imprint","INTERSECT",VERTEX,{"derivedFrom":[subQ5,subQ3]});Q3=makeQuery(id+"F3.imprint","IMPRINT",FACE,{"disambiguationData":[TD([[makeQuery(id+"F3.imprint","IMPRINT",EDGE,{"disambiguationData":[TD([[subQ6,1.0]])],"derivedFrom":subQ5}),-1.0]])]});}
            extrude(context, id + "F6", {"entities" : qUnion([Q0, Q1, Q2, Q3]), "operationType" : NewBodyOperationType.ADD, "depth" : getVariable(context, 'Buffer') / 2 + 3 * getVariable(context, 'Buffer'), "offsetDistance" : 25 * mm});
        }
        {
            var Q0;
            Q0=makeQuery(id+"F3.imprint","IMPRINT",FACE,{"disambiguationData":[TD([[makeQuery(id+"F3.imprint","IMPRINT",EDGE,{"derivedFrom":sQuery(id+"F3.wireOp",EDGE,"E4")}),1.0]])]});
            var Q1;
            Q1=makeQuery(id+"F3.imprint","IMPRINT",FACE,{"disambiguationData":[TD([[makeQuery(id+"F3.imprint","IMPRINT",EDGE,{"derivedFrom":sQuery(id+"F3.wireOp",EDGE,"E13.3.4")}),1.0]])]});
            var Q2;
            Q2=makeQuery(id+"F3.imprint","IMPRINT",FACE,{"disambiguationData":[TD([[makeQuery(id+"F3.imprint","IMPRINT",EDGE,{"derivedFrom":sQuery(id+"F3.wireOp",EDGE,"E13.2.4")}),1.0]])]});
            var Q3;
            Q3=makeQuery(id+"F3.imprint","IMPRINT",FACE,{"disambiguationData":[TD([[makeQuery(id+"F3.imprint","IMPRINT",EDGE,{"derivedFrom":sQuery(id+"F3.wireOp",EDGE,"E13.1.4")}),1.0]])]});
            extrude(context, id + "F7", {"entities" : qUnion([Q0, Q1, Q2, Q3]), "operationType" : NewBodyOperationType.REMOVE, "oppositeDirection" : true, "depth" : getVariable(context, 'BushingThickness') / 2, "offsetDistance" : 25 * mm, "hasSecondDirection" : true, "secondDirectionOppositeDirection" : false, "secondDirectionDepth" : getVariable(context, 'BushingThickness') / 2});
        }
        {
            var Q0;
            Q0=qCreatedBy(makeId("Front.planeOp"),FACE);
            var sketch = newSketch(context, id + "F8", { "sketchPlane" : qUnion([Q0])});
            skCircle(sketch, "E16", {"center": v(0, 3) * mm, "radius": 1 * mm});
            skSolve(sketch);
        }
        {
            var Q0;
            Q0=makeQuery(id+"F8.imprint","IMPRINT",FACE,{"disambiguationData":[TD([[makeQuery(id+"F8.imprint","IMPRINT",EDGE,{"derivedFrom":sQuery(id+"F8.wireOp",EDGE,"E16")}),1.0]])]});
            extrude(context, id + "F9", {"entities" : qUnion([Q0]), "operationType" : NewBodyOperationType.REMOVE, "oppositeDirection" : true, "depth" : getVariable(context, 'Diameter') / 2, "offsetDistance" : 25 * mm, "hasSecondDirection" : true, "secondDirectionOppositeDirection" : false, "secondDirectionDepth" : getVariable(context, 'Diameter') / 2});
        }
        {
            var Q0;
            Q0=makeQuery(id+"F4.opExtrude","CAP_FACE",FACE,{"disambiguationData":[OSD([sQuery(id+"F3.wireOp",EDGE,"E0"),sQuery(id+"F3.wireOp",EDGE,"E6"),sQuery(id+"F3.wireOp",EDGE,"E7"),sQuery(id+"F3.wireOp",EDGE,"E8"),sQuery(id+"F3.wireOp",EDGE,"E9"),sQuery(id+"F3.wireOp",EDGE,"E10"),sQuery(id+"F3.wireOp",EDGE,"E11"),sQuery(id+"F3.wireOp",EDGE,"E13.1.0"),sQuery(id+"F3.wireOp",EDGE,"E13.1.1"),sQuery(id+"F3.wireOp",EDGE,"E13.1.5"),sQuery(id+"F3.wireOp",EDGE,"E13.1.6"),sQuery(id+"F3.wireOp",EDGE,"E13.1.7"),sQuery(id+"F3.wireOp",EDGE,"E13.2.0"),sQuery(id+"F3.wireOp",EDGE,"E13.2.1"),sQuery(id+"F3.wireOp",EDGE,"E13.2.5"),sQuery(id+"F3.wireOp",EDGE,"E13.2.6"),sQuery(id+"F3.wireOp",EDGE,"E13.2.7"),sQuery(id+"F3.wireOp",EDGE,"E13.3.0"),sQuery(id+"F3.wireOp",EDGE,"E13.3.1"),sQuery(id+"F3.wireOp",EDGE,"E13.3.5"),sQuery(id+"F3.wireOp",EDGE,"E13.3.6"),sQuery(id+"F3.wireOp",EDGE,"E13.3.7"),sQuery(id+"F3.wireOp",EDGE,"E14"),sQuery(id+"F3.wireOp",EDGE,"E15.1.0"),sQuery(id+"F3.wireOp",EDGE,"E15.2.0"),sQuery(id+"F3.wireOp",EDGE,"E15.3.0")])],"isStart":true});
            var sketch = newSketch(context, id + "F10", { "sketchPlane" : qUnion([Q0])});
            skCircle(sketch, "E17", {"center": v(0, 0) * mm, "radius": 3.4 * mm});
            skCircle(sketch, "E18", {"center": v(0, 0) * mm, "radius": 1.6 * mm});
            skCircle(sketch, "E19", {"center": v(0, 0) * mm, "radius": 1.8 * mm});
            skLineSegment(sketch, "E20", {"start": v(-0.4, 3.38) * mm, "end": v(-0.4, -3.38) * mm});
            skLineSegment(sketch, "E21", {"start": v(0.4, 3.38) * mm, "end": v(0.4, -3.38) * mm});
            skSolve(sketch);
        }
        {
            var Q0;
            {var subQ0=sQuery(id+"F10.wireOp",EDGE,"E20");var subQ1=sQuery(id+"F10.wireOp",EDGE,"E17");var subQ2=makeQuery(id+"F10.imprint","INTERSECT",VERTEX,{"disambiguationData":[OD(0.0)],"derivedFrom":[subQ1,subQ0]});Q0=makeQuery(id+"F10.imprint","IMPRINT",FACE,{"disambiguationData":[TD([[makeQuery(id+"F10.imprint","IMPRINT",EDGE,{"disambiguationData":[TD([[subQ2,-1.0]])],"derivedFrom":subQ1}),1.0]])]});}
            var Q1;
            {var subQ0=sQuery(id+"F10.wireOp",EDGE,"E21");var subQ1=sQuery(id+"F10.wireOp",EDGE,"E17");var subQ2=makeQuery(id+"F10.imprint","INTERSECT",VERTEX,{"disambiguationData":[OD(0.0)],"derivedFrom":[subQ1,subQ0]});Q1=makeQuery(id+"F10.imprint","IMPRINT",FACE,{"disambiguationData":[TD([[makeQuery(id+"F10.imprint","IMPRINT",EDGE,{"disambiguationData":[TD([[subQ2,1.0]])],"derivedFrom":subQ1}),1.0]])]});}
            extrude(context, id + "F11", {"entities" : qUnion([Q0, Q1]), "depth" : -(getVariable(context, 'Buffer') * 4), "offsetDistance" : 25 * mm});
        }
    });
